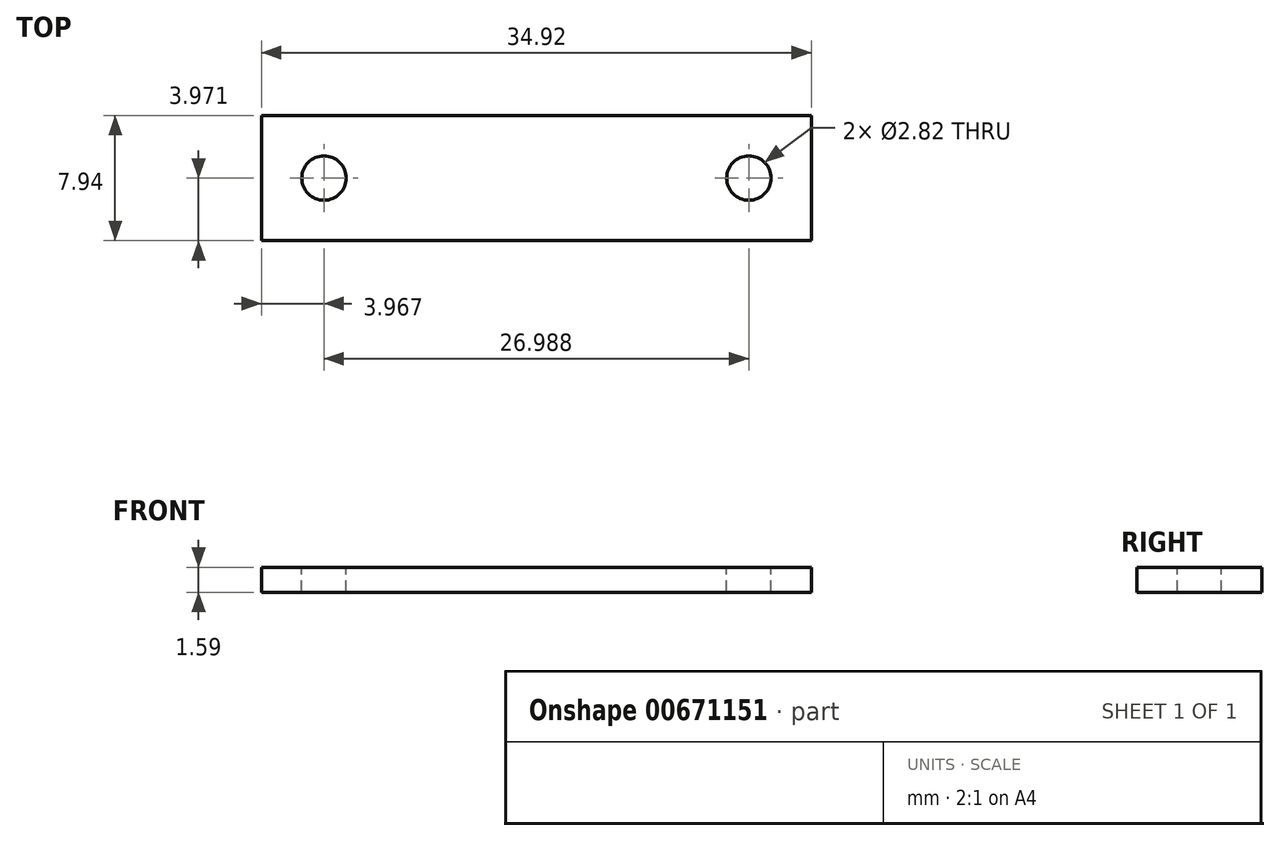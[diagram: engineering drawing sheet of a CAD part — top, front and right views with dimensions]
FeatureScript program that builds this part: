
annotation { "Feature Type Name" : "Feature", "Feature Type Description" : "" }
export const myFeature = defineFeature(function(context is Context, id is Id, definition is map)
    precondition{}
    {
        {
            var Q0;
            Q0=qCreatedBy(makeId("Front.planeOp"),FACE);
            var sketch = newSketch(context, id + "F0", { "sketchPlane" : qUnion([Q0])});
            skLineSegment(sketch, "E0.bottom", {"start": v(10.1, 10.1) * mm, "end": v(45.02, 10.1) * mm});
            skLineSegment(sketch, "E0.top", {"start": v(10.1, 11.69) * mm, "end": v(45.02, 11.69) * mm});
            skLineSegment(sketch, "E0.left", {"start": v(10.1, 10.1) * mm, "end": v(10.1, 11.69) * mm});
            skLineSegment(sketch, "E0.right", {"start": v(45.02, 10.1) * mm, "end": v(45.02, 11.69) * mm});
            skSolve(sketch);
        }
        {
            var Q0;
            Q0=qSketchRegion(id+"F0",true);
            extrude(context, id + "F1", {"entities" : qUnion([Q0]), "depth" : 7.94 * mm});
        }
        {
            var Q0;
            Q0=makeQuery(id+"F1.opExtrude","SWEPT_FACE",FACE,{"disambiguationData":[OSD([sQuery(id+"F0.wireOp",EDGE,"E0.top")])]});
            var sketch = newSketch(context, id + "F2", { "sketchPlane" : qUnion([Q0])});
            skCircle(sketch, "E1", {"center": v(14.07, -3.97) * mm, "radius": 1.4 * mm});
            skCircle(sketch, "E2", {"center": v(41.05, -3.97) * mm, "radius": 1.4 * mm});
            skSolve(sketch);
        }
        {
            var Q0;
            Q0=qSketchRegion(id+"F2",true);
            extrude(context, id + "F3", {"entities" : qUnion([Q0]), "operationType" : NewBodyOperationType.REMOVE, "oppositeDirection" : true, "depth" : 1.59 * mm});
        }
    });
